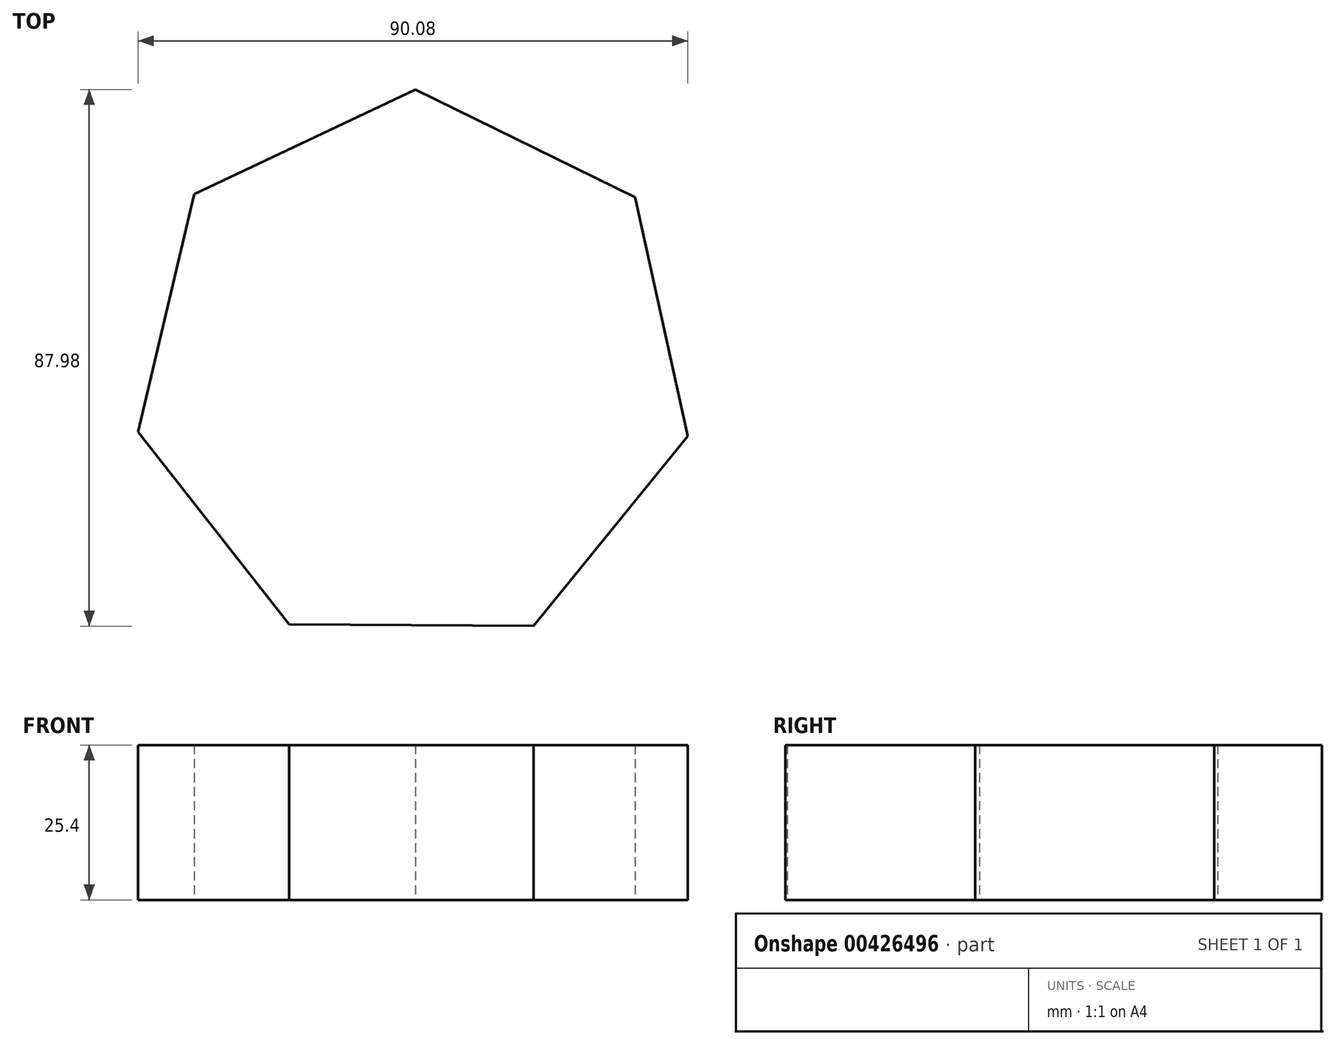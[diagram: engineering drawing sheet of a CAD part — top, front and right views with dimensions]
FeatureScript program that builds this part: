
annotation { "Feature Type Name" : "Feature", "Feature Type Description" : "" }
export const myFeature = defineFeature(function(context is Context, id is Id, definition is map)
    precondition{}
    {
        {
            var Q0;
            Q0=qCreatedBy(makeId("Top.planeOp"),FACE);
            var sketch = newSketch(context, id + "F0", { "sketchPlane" : qUnion([Q0])});
            skCircle(sketch, "E0.cCircle", {"center": v(0, 0) * mm, "radius": 41.62 * mm, "construction": true});
            skLineSegment(sketch, "E0.0", {"start": v(44.96, -10.63) * mm, "end": v(19.72, -41.78) * mm});
            skLineSegment(sketch, "E0.1", {"start": v(19.72, -41.78) * mm, "end": v(-20.36, -41.47) * mm});
            skLineSegment(sketch, "E0.2", {"start": v(-20.36, -41.47) * mm, "end": v(-45.12, -9.93) * mm});
            skLineSegment(sketch, "E0.3", {"start": v(-45.12, -9.93) * mm, "end": v(-35.9, 29.08) * mm});
            skLineSegment(sketch, "E0.4", {"start": v(-35.9, 29.08) * mm, "end": v(0.35, 46.2) * mm});
            skLineSegment(sketch, "E0.5", {"start": v(0.35, 46.2) * mm, "end": v(36.34, 28.53) * mm});
            skLineSegment(sketch, "E0.6", {"start": v(36.34, 28.53) * mm, "end": v(44.96, -10.63) * mm});
            skPoint(sketch, "E0.0.midPoint", {"position": v(32.34, -26.2) * mm});
            skSolve(sketch);
        }
        {
            var Q0;
            Q0=makeQuery(id+"F0.imprint","IMPRINT",FACE,{"disambiguationData":[TD([[makeQuery(id+"F0.imprint","IMPRINT",EDGE,{"derivedFrom":sQuery(id+"F0.wireOp",EDGE,"E0.0")}),-1.0]])]});
            extrude(context, id + "F1", {"entities" : qUnion([Q0]), "depth" : 25.4 * mm});
        }
        {
            var Q1;
            Q1=makeQuery(id+"F1.opExtrude","CAP_FACE",FACE,{"disambiguationData":[OSD([sQuery(id+"F0.wireOp",EDGE,"E0.0"),sQuery(id+"F0.wireOp",EDGE,"E0.1"),sQuery(id+"F0.wireOp",EDGE,"E0.2"),sQuery(id+"F0.wireOp",EDGE,"E0.3"),sQuery(id+"F0.wireOp",EDGE,"E0.4"),sQuery(id+"F0.wireOp",EDGE,"E0.5"),sQuery(id+"F0.wireOp",EDGE,"E0.6")])],"isStart":false});
            var Q2;
            Q2=makeQuery(id+"F1.opExtrude","CAP_FACE",FACE,{"disambiguationData":[OSD([sQuery(id+"F0.wireOp",EDGE,"E0.0"),sQuery(id+"F0.wireOp",EDGE,"E0.1"),sQuery(id+"F0.wireOp",EDGE,"E0.2"),sQuery(id+"F0.wireOp",EDGE,"E0.3"),sQuery(id+"F0.wireOp",EDGE,"E0.4"),sQuery(id+"F0.wireOp",EDGE,"E0.5"),sQuery(id+"F0.wireOp",EDGE,"E0.6")])],"isStart":true});
            loft(context, id + "F2", {"operationType" : NewBodyOperationType.ADD, "sheetProfilesArray" : [{ "sheetProfileEntities" : qUnion([Q1]) }, { "sheetProfileEntities" : qUnion([Q2]) }]});
        }
    });
